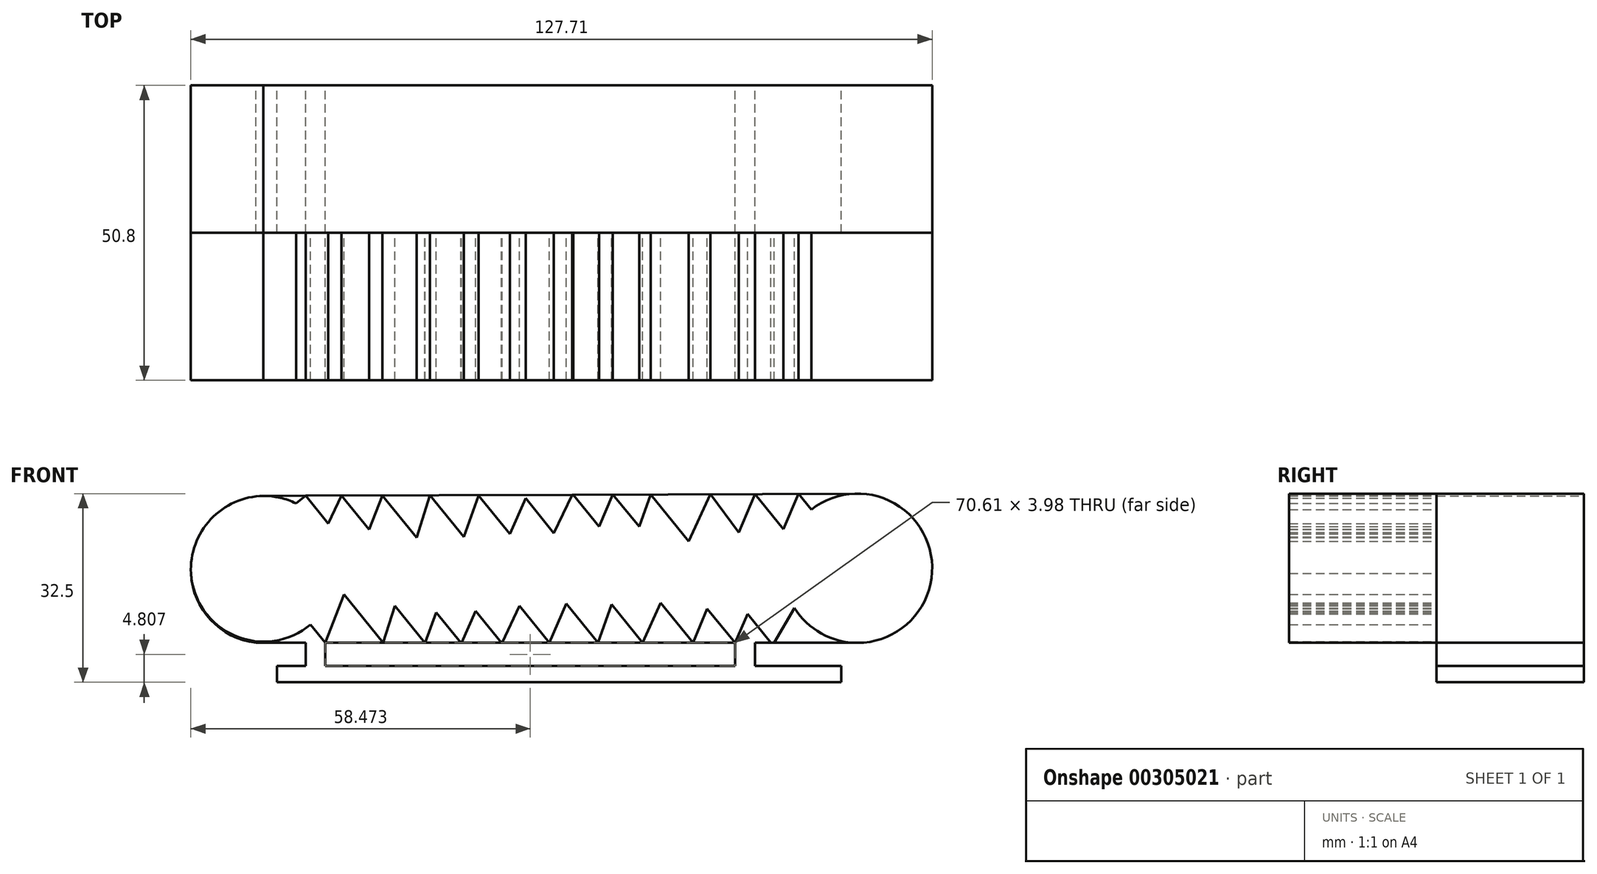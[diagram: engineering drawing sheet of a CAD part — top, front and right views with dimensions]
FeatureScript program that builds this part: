
annotation { "Feature Type Name" : "Feature", "Feature Type Description" : "" }
export const myFeature = defineFeature(function(context is Context, id is Id, definition is map)
    precondition{}
    {
        {
            var Q0;
            Q0=qCreatedBy(makeId("Front.planeOp"),FACE);
            var sketch = newSketch(context, id + "F0", { "sketchPlane" : qUnion([Q0])});
            skArc(sketch, "E0", {"start": v(-84.7, 31) * mm, "mid": v(-97.17, 18.95) * mm, "end": v(-85.99, 5.69) * mm});
            skLineSegment(sketch, "E1", {"start": v(-84.7, 31) * mm, "end": v(17.62, 31.4) * mm});
            skLineSegment(sketch, "E2", {"start": v(17.72, 5.69) * mm, "end": v(-85.99, 5.69) * mm});
            skArc(sketch, "E3", {"start": v(17.72, 5.69) * mm, "mid": v(30.52, 18.6) * mm, "end": v(17.62, 31.4) * mm});
            skLineSegment(sketch, "E4.bottom", {"start": v(-82.38, 1.7) * mm, "end": v(14.86, 1.7) * mm});
            skLineSegment(sketch, "E4.top", {"start": v(-82.38, -1.11) * mm, "end": v(14.86, -1.11) * mm});
            skLineSegment(sketch, "E4.left", {"start": v(-82.38, 1.7) * mm, "end": v(-82.38, -1.11) * mm});
            skLineSegment(sketch, "E4.right", {"start": v(14.86, 1.7) * mm, "end": v(14.86, -1.11) * mm});
            skLineSegment(sketch, "E5", {"start": v(-77.4, 5.69) * mm, "end": v(-77.4, 1.7) * mm});
            skLineSegment(sketch, "E6", {"start": v(-74.02, 5.69) * mm, "end": v(-74.02, 1.7) * mm});
            skLineSegment(sketch, "E7", {"start": v(-3.41, 5.69) * mm, "end": v(-3.41, 1.7) * mm});
            skLineSegment(sketch, "E8", {"start": v(0, 5.69) * mm, "end": v(0, 1.7) * mm});
            skSolve(sketch);
        }
        {
            var Q0;
            {var subQ4=sQuery(id+"F0.wireOp",EDGE,"E0");Q0=makeQuery(id+"F0.imprint","IMPRINT",FACE,{"disambiguationData":[TD([[makeQuery(id+"F0.imprint","IMPRINT",EDGE,{"derivedFrom":subQ4}),1.0]])]});}
            var Q1;
            Q1=makeQuery(id+"F0.imprint","IMPRINT",FACE,{"disambiguationData":[TD([[makeQuery(id+"F0.imprint","IMPRINT",EDGE,{"derivedFrom":sQuery(id+"F0.wireOp",EDGE,"E4.top")}),1.0]])]});
            var Q2;
            {var subQ0=sQuery(id+"F0.wireOp",EDGE,"E5");Q2=makeQuery(id+"F0.imprint","IMPRINT",FACE,{"disambiguationData":[TD([[makeQuery(id+"F0.imprint","IMPRINT",EDGE,{"derivedFrom":subQ0}),1.0]])]});}
            var Q3;
            {var subQ0=sQuery(id+"F0.wireOp",EDGE,"E7");Q3=makeQuery(id+"F0.imprint","IMPRINT",FACE,{"disambiguationData":[TD([[makeQuery(id+"F0.imprint","IMPRINT",EDGE,{"derivedFrom":subQ0}),1.0]])]});}
            extrude(context, id + "F1", {"entities" : qUnion([Q0, Q1, Q2, Q3]), "depth" : 25.4 * mm});
        }
        {
            var Q0;
            Q0=makeQuery(id+"F1.opExtrude","CAP_FACE",FACE,{"disambiguationData":[OSD([sQuery(id+"F0.wireOp",EDGE,"E0"),sQuery(id+"F0.wireOp",EDGE,"E1"),sQuery(id+"F0.wireOp",EDGE,"E2"),sQuery(id+"F0.wireOp",EDGE,"E3"),sQuery(id+"F0.wireOp",EDGE,"E4.bottom"),sQuery(id+"F0.wireOp",EDGE,"E4.top"),sQuery(id+"F0.wireOp",EDGE,"E4.left"),sQuery(id+"F0.wireOp",EDGE,"E4.right"),sQuery(id+"F0.wireOp",EDGE,"E5"),sQuery(id+"F0.wireOp",EDGE,"E6"),sQuery(id+"F0.wireOp",EDGE,"E7"),sQuery(id+"F0.wireOp",EDGE,"E8")])],"isStart":false});
            var sketch = newSketch(context, id + "F2", { "sketchPlane" : qUnion([Q0])});
            skArc(sketch, "E9", {"start": v(-97.17, 17.65) * mm, "mid": v(-75.47, 9.86) * mm, "end": v(-84.7, 31) * mm});
            skPoint(sketch, "E9.startSnap0", {"position": v(-97.17, 18.95) * mm});
            skArc(sketch, "E10", {"start": v(17.62, 31.4) * mm, "mid": v(10.72, 29.35) * mm, "end": v(6, 23.92) * mm});
            skPoint(sketch, "E10.endSnap0", {"position": v(30.52, 18.6) * mm});
            skLineSegment(sketch, "E11", {"start": v(-71.22, 31.05) * mm, "end": v(-50.7, 5.69) * mm});
            skLineSegment(sketch, "E12", {"start": v(-64.2, 31.08) * mm, "end": v(-43.65, 5.69) * mm});
            skLineSegment(sketch, "E13", {"start": v(-56, 31.1) * mm, "end": v(-35.42, 5.69) * mm});
            skLineSegment(sketch, "E14", {"start": v(-47.65, 31.14) * mm, "end": v(-27.06, 5.69) * mm});
            skLineSegment(sketch, "E15", {"start": v(-39.99, 31.17) * mm, "end": v(-19.37, 5.69) * mm});
            skLineSegment(sketch, "E16", {"start": v(-31.32, 31.2) * mm, "end": v(-10.67, 5.69) * mm});
            skPoint(sketch, "E17.end.orphan", {"position": v(-22.03, 31) * mm});
            skLineSegment(sketch, "E18", {"start": v(-24.5, 31.23) * mm, "end": v(-3.41, 5.69) * mm});
            skLineSegment(sketch, "E19", {"start": v(-17.95, 31.26) * mm, "end": v(2.74, 5.69) * mm});
            skLineSegment(sketch, "E20", {"start": v(-7.69, 31.3) * mm, "end": v(6.51, 12.15) * mm});
            skLineSegment(sketch, "E21", {"start": v(0, 31.33) * mm, "end": v(6, 23.92) * mm});
            skLineSegment(sketch, "E22", {"start": v(7.48, 31.35) * mm, "end": v(9.7, 28.62) * mm});
            skLineSegment(sketch, "E23", {"start": v(-77.4, 31.05) * mm, "end": v(-56.88, 5.69) * mm});
            skPoint(sketch, "E23.startSnap0", {"position": v(-77.4, 3.7) * mm});
            skLineSegment(sketch, "E24", {"start": v(-72.34, 15.93) * mm, "end": v(-64.05, 5.69) * mm});
            skLineSegment(sketch, "E25", {"start": v(-77.4, 9.86) * mm, "end": v(-74.02, 5.69) * mm});
            skPoint(sketch, "E25.startSnap0", {"position": v(-75.47, 9.86) * mm});
            skLineSegment(sketch, "E26", {"start": v(0, 31.33) * mm, "end": v(-10.67, 5.69) * mm});
            skLineSegment(sketch, "E27", {"start": v(-7.69, 31.3) * mm, "end": v(-19.37, 5.69) * mm});
            skLineSegment(sketch, "E28", {"start": v(-17.95, 31.26) * mm, "end": v(-27.06, 5.69) * mm});
            skLineSegment(sketch, "E29", {"start": v(-24.5, 31.23) * mm, "end": v(-35.42, 5.69) * mm});
            skLineSegment(sketch, "E30", {"start": v(-31.43, 31.4) * mm, "end": v(-43.65, 5.51) * mm});
            skLineSegment(sketch, "E31", {"start": v(-39.18, 31.29) * mm, "end": v(-50.69, 5.35) * mm});
            skLineSegment(sketch, "E32", {"start": v(-47.53, 31.26) * mm, "end": v(-56.96, 5.33) * mm});
            skLineSegment(sketch, "E33", {"start": v(6.9, 11.88) * mm, "end": v(3.07, 5.3) * mm});
            skLineSegment(sketch, "E34", {"start": v(6.44, 24.24) * mm, "end": v(5.34, 22.18) * mm});
            skLineSegment(sketch, "E35", {"start": v(-56, 31.1) * mm, "end": v(-64.05, 5.69) * mm});
            skLineSegment(sketch, "E36", {"start": v(-64.2, 31.08) * mm, "end": v(-74.02, 5.69) * mm});
            skPoint(sketch, "E37.end.orphan", {"position": v(-72.34, 22.47) * mm});
            skPoint(sketch, "E38.trimOffspring.end.orphan", {"position": v(-74.02, 25.13) * mm});
            skPoint(sketch, "E39.end.orphan", {"position": v(-74.02, 22.7) * mm});
            skLineSegment(sketch, "E40", {"start": v(-71.22, 31.05) * mm, "end": v(-74.02, 25.13) * mm});
            skLineSegment(sketch, "E41", {"start": v(-77.4, 31.05) * mm, "end": v(-79.08, 29.7) * mm});
            skArc(sketch, "E42.trimOffspring", {"start": v(5.34, 22.18) * mm, "mid": v(15.8, 5.82) * mm, "end": v(30.52, 18.5) * mm});
            skLineSegment(sketch, "E43", {"start": v(7.48, 31.35) * mm, "end": v(-3.41, 5.69) * mm});
            skSolve(sketch);
        }
        {
            var Q0;
            {var subQ3=sQuery(id+"F2.wireOp",EDGE,"E22");Q0=makeQuery(id+"F2.imprint","IMPRINT",FACE,{"disambiguationData":[TD([[makeQuery(id+"F2.imprint","IMPRINT",EDGE,{"derivedFrom":subQ3}),-1.0]])]});}
            var Q1;
            {var subQ0=sQuery(id+"F2.wireOp",EDGE,"E24");var subQ1=sQuery(id+"F2.wireOp",EDGE,"E9");var subQ2=makeQuery(id+"F2.imprint","INTERSECT",VERTEX,{"derivedFrom":[subQ1,subQ0]});Q1=makeQuery(id+"F2.imprint","IMPRINT",FACE,{"disambiguationData":[TD([[makeQuery(id+"F2.imprint","IMPRINT",EDGE,{"disambiguationData":[TD([[subQ2,1.0]])],"derivedFrom":subQ1}),-1.0]])]});}
            var Q2;
            {var subQ0=sQuery(id+"F2.wireOp",EDGE,"E40");var subQ5=sQuery(id+"F2.wireOp",EDGE,"E23");var subQ6=makeQuery(id+"F2.imprint","INTERSECT",VERTEX,{"derivedFrom":[subQ5,subQ0]});Q2=makeQuery(id+"F2.imprint","IMPRINT",FACE,{"disambiguationData":[TD([[makeQuery(id+"F2.imprint","IMPRINT",EDGE,{"disambiguationData":[TD([[subQ6,-1.0]])],"derivedFrom":subQ5}),1.0]])]});}
            var Q3;
            {var subQ0=sQuery(id+"F2.wireOp",EDGE,"E36");var subQ1=sQuery(id+"F2.wireOp",EDGE,"E11");var subQ2=makeQuery(id+"F2.imprint","INTERSECT",VERTEX,{"derivedFrom":[subQ1,subQ0]});Q3=makeQuery(id+"F2.imprint","IMPRINT",FACE,{"disambiguationData":[TD([[makeQuery(id+"F2.imprint","IMPRINT",EDGE,{"disambiguationData":[TD([[subQ2,-1.0]])],"derivedFrom":subQ1}),1.0]])]});}
            var Q4;
            {var subQ0=sQuery(id+"F2.wireOp",EDGE,"E36");var subQ1=sQuery(id+"F2.wireOp",EDGE,"E11");var subQ2=makeQuery(id+"F2.imprint","INTERSECT",VERTEX,{"derivedFrom":[subQ1,subQ0]});Q4=makeQuery(id+"F2.imprint","IMPRINT",FACE,{"disambiguationData":[TD([[makeQuery(id+"F2.imprint","IMPRINT",EDGE,{"disambiguationData":[TD([[subQ2,-1.0]])],"derivedFrom":subQ1}),-1.0]])]});}
            var Q5;
            {var subQ0=sQuery(id+"F2.wireOp",EDGE,"E35");var subQ1=sQuery(id+"F2.wireOp",EDGE,"E11");var subQ2=makeQuery(id+"F2.imprint","INTERSECT",VERTEX,{"derivedFrom":[subQ1,subQ0]});Q5=makeQuery(id+"F2.imprint","IMPRINT",FACE,{"disambiguationData":[TD([[makeQuery(id+"F2.imprint","IMPRINT",EDGE,{"disambiguationData":[TD([[subQ2,-1.0]])],"derivedFrom":subQ1}),1.0]])]});}
            var Q6;
            {var subQ0=sQuery(id+"F2.wireOp",EDGE,"E35");var subQ1=sQuery(id+"F2.wireOp",EDGE,"E12");var subQ2=makeQuery(id+"F2.imprint","INTERSECT",VERTEX,{"derivedFrom":[subQ1,subQ0]});Q6=makeQuery(id+"F2.imprint","IMPRINT",FACE,{"disambiguationData":[TD([[makeQuery(id+"F2.imprint","IMPRINT",EDGE,{"disambiguationData":[TD([[subQ2,-1.0]])],"derivedFrom":subQ1}),1.0]])]});}
            var Q7;
            {var subQ0=sQuery(id+"F2.wireOp",EDGE,"E32");var subQ1=sQuery(id+"F2.wireOp",EDGE,"E12");var subQ2=makeQuery(id+"F2.imprint","INTERSECT",VERTEX,{"derivedFrom":[subQ1,subQ0]});Q7=makeQuery(id+"F2.imprint","IMPRINT",FACE,{"disambiguationData":[TD([[makeQuery(id+"F2.imprint","IMPRINT",EDGE,{"disambiguationData":[TD([[subQ2,-1.0]])],"derivedFrom":subQ1}),1.0]])]});}
            var Q8;
            {var subQ0=sQuery(id+"F2.wireOp",EDGE,"E32");var subQ1=sQuery(id+"F2.wireOp",EDGE,"E13");var subQ2=makeQuery(id+"F2.imprint","INTERSECT",VERTEX,{"derivedFrom":[subQ1,subQ0]});Q8=makeQuery(id+"F2.imprint","IMPRINT",FACE,{"disambiguationData":[TD([[makeQuery(id+"F2.imprint","IMPRINT",EDGE,{"disambiguationData":[TD([[subQ2,-1.0]])],"derivedFrom":subQ1}),1.0]])]});}
            var Q9;
            {var subQ0=sQuery(id+"F2.wireOp",EDGE,"E31");var subQ1=sQuery(id+"F2.wireOp",EDGE,"E13");var subQ2=makeQuery(id+"F2.imprint","INTERSECT",VERTEX,{"derivedFrom":[subQ1,subQ0]});Q9=makeQuery(id+"F2.imprint","IMPRINT",FACE,{"disambiguationData":[TD([[makeQuery(id+"F2.imprint","IMPRINT",EDGE,{"disambiguationData":[TD([[subQ2,-1.0]])],"derivedFrom":subQ1}),1.0]])]});}
            var Q10;
            {var subQ4=sQuery(id+"F2.wireOp",EDGE,"E30");var subQ6=sQuery(id+"F2.wireOp",EDGE,"E14");var subQ7=makeQuery(id+"F2.imprint","INTERSECT",VERTEX,{"derivedFrom":[subQ6,subQ4]});Q10=makeQuery(id+"F2.imprint","IMPRINT",FACE,{"disambiguationData":[TD([[makeQuery(id+"F2.imprint","IMPRINT",EDGE,{"disambiguationData":[TD([[subQ7,-1.0]])],"derivedFrom":subQ6}),-1.0]])]});}
            var Q11;
            {var subQ0=sQuery(id+"F2.wireOp",EDGE,"E31");var subQ1=sQuery(id+"F2.wireOp",EDGE,"E14");var subQ2=makeQuery(id+"F2.imprint","INTERSECT",VERTEX,{"derivedFrom":[subQ1,subQ0]});Q11=makeQuery(id+"F2.imprint","IMPRINT",FACE,{"disambiguationData":[TD([[makeQuery(id+"F2.imprint","IMPRINT",EDGE,{"disambiguationData":[TD([[subQ2,-1.0]])],"derivedFrom":subQ1}),1.0]])]});}
            var Q12;
            {var subQ0=sQuery(id+"F2.wireOp",EDGE,"E30");var subQ1=sQuery(id+"F2.wireOp",EDGE,"E14");var subQ2=makeQuery(id+"F2.imprint","INTERSECT",VERTEX,{"derivedFrom":[subQ1,subQ0]});Q12=makeQuery(id+"F2.imprint","IMPRINT",FACE,{"disambiguationData":[TD([[makeQuery(id+"F2.imprint","IMPRINT",EDGE,{"disambiguationData":[TD([[subQ2,-1.0]])],"derivedFrom":subQ1}),1.0]])]});}
            var Q13;
            {var subQ4=sQuery(id+"F2.wireOp",EDGE,"E29");var subQ6=sQuery(id+"F2.wireOp",EDGE,"E15");var subQ7=makeQuery(id+"F2.imprint","INTERSECT",VERTEX,{"derivedFrom":[subQ6,subQ4]});Q13=makeQuery(id+"F2.imprint","IMPRINT",FACE,{"disambiguationData":[TD([[makeQuery(id+"F2.imprint","IMPRINT",EDGE,{"disambiguationData":[TD([[subQ7,-1.0]])],"derivedFrom":subQ6}),-1.0]])]});}
            var Q14;
            {var subQ0=sQuery(id+"F2.wireOp",EDGE,"E29");var subQ1=sQuery(id+"F2.wireOp",EDGE,"E15");var subQ2=makeQuery(id+"F2.imprint","INTERSECT",VERTEX,{"derivedFrom":[subQ1,subQ0]});Q14=makeQuery(id+"F2.imprint","IMPRINT",FACE,{"disambiguationData":[TD([[makeQuery(id+"F2.imprint","IMPRINT",EDGE,{"disambiguationData":[TD([[subQ2,-1.0]])],"derivedFrom":subQ1}),1.0]])]});}
            var Q15;
            {var subQ0=sQuery(id+"F2.wireOp",EDGE,"E29");var subQ1=sQuery(id+"F2.wireOp",EDGE,"E16");var subQ2=makeQuery(id+"F2.imprint","INTERSECT",VERTEX,{"derivedFrom":[subQ1,subQ0]});Q15=makeQuery(id+"F2.imprint","IMPRINT",FACE,{"disambiguationData":[TD([[makeQuery(id+"F2.imprint","IMPRINT",EDGE,{"disambiguationData":[TD([[subQ2,-1.0]])],"derivedFrom":subQ1}),1.0]])]});}
            var Q16;
            {var subQ0=sQuery(id+"F2.wireOp",EDGE,"E27");var subQ1=sQuery(id+"F2.wireOp",EDGE,"E16");var subQ2=makeQuery(id+"F2.imprint","INTERSECT",VERTEX,{"derivedFrom":[subQ1,subQ0]});Q16=makeQuery(id+"F2.imprint","IMPRINT",FACE,{"disambiguationData":[TD([[makeQuery(id+"F2.imprint","IMPRINT",EDGE,{"disambiguationData":[TD([[subQ2,1.0]])],"derivedFrom":subQ1}),1.0]])]});}
            var Q17;
            {var subQ4=sQuery(id+"F2.wireOp",EDGE,"E27");var subQ6=sQuery(id+"F2.wireOp",EDGE,"E18");var subQ7=makeQuery(id+"F2.imprint","INTERSECT",VERTEX,{"derivedFrom":[subQ6,subQ4]});Q17=makeQuery(id+"F2.imprint","IMPRINT",FACE,{"disambiguationData":[TD([[makeQuery(id+"F2.imprint","IMPRINT",EDGE,{"disambiguationData":[TD([[subQ7,-1.0]])],"derivedFrom":subQ6}),-1.0]])]});}
            var Q18;
            {var subQ0=sQuery(id+"F2.wireOp",EDGE,"E28");var subQ1=sQuery(id+"F2.wireOp",EDGE,"E18");var subQ2=makeQuery(id+"F2.imprint","INTERSECT",VERTEX,{"derivedFrom":[subQ1,subQ0]});Q18=makeQuery(id+"F2.imprint","IMPRINT",FACE,{"disambiguationData":[TD([[makeQuery(id+"F2.imprint","IMPRINT",EDGE,{"disambiguationData":[TD([[subQ2,-1.0]])],"derivedFrom":subQ1}),1.0]])]});}
            var Q19;
            {var subQ0=sQuery(id+"F2.wireOp",EDGE,"E27");var subQ1=sQuery(id+"F2.wireOp",EDGE,"E18");var subQ2=makeQuery(id+"F2.imprint","INTERSECT",VERTEX,{"derivedFrom":[subQ1,subQ0]});Q19=makeQuery(id+"F2.imprint","IMPRINT",FACE,{"disambiguationData":[TD([[makeQuery(id+"F2.imprint","IMPRINT",EDGE,{"disambiguationData":[TD([[subQ2,-1.0]])],"derivedFrom":subQ1}),1.0]])]});}
            var Q20;
            {var subQ5=sQuery(id+"F2.wireOp",EDGE,"E26");var subQ7=sQuery(id+"F2.wireOp",EDGE,"E19");var subQ8=makeQuery(id+"F2.imprint","INTERSECT",VERTEX,{"derivedFrom":[subQ7,subQ5]});Q20=makeQuery(id+"F2.imprint","IMPRINT",FACE,{"disambiguationData":[TD([[makeQuery(id+"F2.imprint","IMPRINT",EDGE,{"disambiguationData":[TD([[subQ8,-1.0]])],"derivedFrom":subQ7}),-1.0]])]});}
            var Q21;
            {var subQ0=sQuery(id+"F2.wireOp",EDGE,"E27");var subQ1=sQuery(id+"F2.wireOp",EDGE,"E19");var subQ2=makeQuery(id+"F2.imprint","INTERSECT",VERTEX,{"derivedFrom":[subQ1,subQ0]});Q21=makeQuery(id+"F2.imprint","IMPRINT",FACE,{"disambiguationData":[TD([[makeQuery(id+"F2.imprint","IMPRINT",EDGE,{"disambiguationData":[TD([[subQ2,-1.0]])],"derivedFrom":subQ1}),1.0]])]});}
            var Q22;
            {var subQ0=sQuery(id+"F2.wireOp",EDGE,"E26");var subQ1=sQuery(id+"F2.wireOp",EDGE,"E20");var subQ2=makeQuery(id+"F2.imprint","INTERSECT",VERTEX,{"derivedFrom":[subQ1,subQ0]});Q22=makeQuery(id+"F2.imprint","IMPRINT",FACE,{"disambiguationData":[TD([[makeQuery(id+"F2.imprint","IMPRINT",EDGE,{"disambiguationData":[TD([[subQ2,-1.0]])],"derivedFrom":subQ1}),1.0]])]});}
            var Q23;
            {var subQ0=sQuery(id+"F2.wireOp",EDGE,"E36");var subQ1=sQuery(id+"F2.wireOp",EDGE,"E23");var subQ2=makeQuery(id+"F2.imprint","INTERSECT",VERTEX,{"derivedFrom":[subQ1,subQ0]});Q23=makeQuery(id+"F2.imprint","IMPRINT",FACE,{"disambiguationData":[TD([[makeQuery(id+"F2.imprint","IMPRINT",EDGE,{"disambiguationData":[TD([[subQ2,-1.0]])],"derivedFrom":subQ1}),-1.0]])]});}
            var Q24;
            {var subQ3=sQuery(id+"F2.wireOp",EDGE,"E24");var subQ7=sQuery(id+"F2.wireOp",EDGE,"E9");var subQ8=makeQuery(id+"F2.imprint","INTERSECT",VERTEX,{"derivedFrom":[subQ7,subQ3]});Q24=makeQuery(id+"F2.imprint","IMPRINT",FACE,{"disambiguationData":[TD([[makeQuery(id+"F2.imprint","IMPRINT",EDGE,{"disambiguationData":[TD([[subQ8,-1.0]])],"derivedFrom":subQ7}),-1.0]])]});}
            var Q25;
            {var subQ0=sQuery(id+"F2.wireOp",EDGE,"E41");var subQ1=sQuery(id+"F2.wireOp",EDGE,"E23");var subQ2=makeQuery(id+"F2.imprint","INTERSECT",VERTEX,{"derivedFrom":[subQ1,subQ0]});Q25=makeQuery(id+"F2.imprint","IMPRINT",FACE,{"disambiguationData":[TD([[makeQuery(id+"F2.imprint","IMPRINT",EDGE,{"disambiguationData":[TD([[subQ2,-1.0]])],"derivedFrom":subQ1}),-1.0]])]});}
            var Q26;
            {var subQ0=sQuery(id+"F2.wireOp",EDGE,"E42.trimOffspring");var subQ1=sQuery(id+"F0.wireOp",EDGE,"E2");var subQ2=makeQuery(id+"F1.opExtrude","CAP_EDGE",EDGE,{"disambiguationData":[OSD([subQ1]),TDD([makeQuery(id+"F0.imprint","IMPRINT",EDGE,{"disambiguationData":[TD([[makeQuery(id+"F0.imprint","INTERSECT",VERTEX,{"derivedFrom":[subQ1,sQuery(id+"F0.wireOp",EDGE,"E3")]}),-1.0]])],"derivedFrom":subQ1})])],"isStart":false});var subQ3=makeQuery(id+"F2.imprint","INTERSECT",VERTEX,{"disambiguationData":[OD(0.0)],"derivedFrom":[subQ2,subQ0]});Q26=makeQuery(id+"F2.imprint","IMPRINT",FACE,{"disambiguationData":[TD([[makeQuery(id+"F2.imprint","IMPRINT",EDGE,{"disambiguationData":[TD([[subQ3,1.0]])],"derivedFrom":subQ0}),1.0]])]});}
            var Q27;
            {var subQ1=sQuery(id+"F2.wireOp",EDGE,"E9");var subQ5=sQuery(id+"F2.wireOp",EDGE,"E40");var subQ6=makeQuery(id+"F2.imprint","INTERSECT",VERTEX,{"derivedFrom":[subQ1,subQ5]});Q27=makeQuery(id+"F2.imprint","IMPRINT",FACE,{"disambiguationData":[TD([[makeQuery(id+"F2.imprint","IMPRINT",EDGE,{"disambiguationData":[TD([[subQ6,-1.0]])],"derivedFrom":subQ1}),-1.0]])]});}
            var Q28;
            {var subQ6=sQuery(id+"F2.wireOp",EDGE,"E21");var subQ7=sQuery(id+"F2.wireOp",EDGE,"E10");var subQ8=makeQuery(id+"F2.imprint","INTERSECT",VERTEX,{"derivedFrom":[subQ7,subQ6]});Q28=makeQuery(id+"F2.imprint","IMPRINT",FACE,{"disambiguationData":[TD([[makeQuery(id+"F2.imprint","IMPRINT",EDGE,{"disambiguationData":[TD([[subQ8,1.0]])],"derivedFrom":subQ7}),1.0]])]});}
            var Q29;
            {var subQ0=sQuery(id+"F2.wireOp",EDGE,"E9");var subQ5=makeQuery(id+"F1.opExtrude","CAP_EDGE",EDGE,{"disambiguationData":[OSD([sQuery(id+"F0.wireOp",EDGE,"E0")])],"isStart":false});var subQ6=makeQuery(id+"F2.imprint","INTERSECT",VERTEX,{"derivedFrom":[subQ5,subQ0]});Q29=makeQuery(id+"F2.imprint","IMPRINT",FACE,{"disambiguationData":[TD([[makeQuery(id+"F2.imprint","IMPRINT",EDGE,{"disambiguationData":[TD([[subQ6,-1.0]])],"derivedFrom":subQ0}),1.0]])]});}
            var Q30;
            {var subQ0=sQuery(id+"F2.wireOp",EDGE,"E35");var subQ1=sQuery(id+"F2.wireOp",EDGE,"E11");var subQ2=makeQuery(id+"F2.imprint","INTERSECT",VERTEX,{"derivedFrom":[subQ1,subQ0]});Q30=makeQuery(id+"F2.imprint","IMPRINT",FACE,{"disambiguationData":[TD([[makeQuery(id+"F2.imprint","IMPRINT",EDGE,{"disambiguationData":[TD([[subQ2,-1.0]])],"derivedFrom":subQ1}),-1.0]])]});}
            var Q31;
            {var subQ0=sQuery(id+"F2.wireOp",EDGE,"E32");var subQ3=sQuery(id+"F2.wireOp",EDGE,"E12");var subQ4=makeQuery(id+"F2.imprint","INTERSECT",VERTEX,{"derivedFrom":[subQ3,subQ0]});Q31=makeQuery(id+"F2.imprint","IMPRINT",FACE,{"disambiguationData":[TD([[makeQuery(id+"F2.imprint","IMPRINT",EDGE,{"disambiguationData":[TD([[subQ4,-1.0]])],"derivedFrom":subQ3}),-1.0]])]});}
            var Q32;
            {var subQ1=sQuery(id+"F2.wireOp",EDGE,"E13");var subQ6=sQuery(id+"F2.wireOp",EDGE,"E31");var subQ9=makeQuery(id+"F2.imprint","INTERSECT",VERTEX,{"derivedFrom":[subQ1,subQ6]});Q32=makeQuery(id+"F2.imprint","IMPRINT",FACE,{"disambiguationData":[TD([[makeQuery(id+"F2.imprint","IMPRINT",EDGE,{"disambiguationData":[TD([[subQ9,-1.0]])],"derivedFrom":subQ1}),-1.0]])]});}
            var Q33;
            {var subQ0=sQuery(id+"F2.wireOp",EDGE,"E42.trimOffspring");var subQ10=sQuery(id+"F2.wireOp",EDGE,"E20");var subQ11=makeQuery(id+"F2.imprint","INTERSECT",VERTEX,{"derivedFrom":[subQ10,subQ0]});Q33=makeQuery(id+"F2.imprint","IMPRINT",FACE,{"disambiguationData":[TD([[makeQuery(id+"F2.imprint","IMPRINT",EDGE,{"disambiguationData":[TD([[subQ11,1.0]])],"derivedFrom":subQ10}),-1.0]])]});}
            var Q34;
            {var subQ0=sQuery(id+"F2.wireOp",EDGE,"E26");var subQ1=sQuery(id+"F2.wireOp",EDGE,"E19");var subQ2=makeQuery(id+"F2.imprint","INTERSECT",VERTEX,{"derivedFrom":[subQ1,subQ0]});Q34=makeQuery(id+"F2.imprint","IMPRINT",FACE,{"disambiguationData":[TD([[makeQuery(id+"F2.imprint","IMPRINT",EDGE,{"disambiguationData":[TD([[subQ2,-1.0]])],"derivedFrom":subQ1}),1.0]])]});}
            var Q35;
            {var subQ3=sQuery(id+"F2.wireOp",EDGE,"E16");var subQ5=makeQuery(id+"F2.imprint","INTERSECT",VERTEX,{"derivedFrom":[subQ3,sQuery(id+"F2.wireOp",EDGE,"E27")]});Q35=makeQuery(id+"F2.imprint","IMPRINT",FACE,{"disambiguationData":[TD([[makeQuery(id+"F2.imprint","IMPRINT",EDGE,{"disambiguationData":[TD([[subQ5,1.0]])],"derivedFrom":subQ3}),-1.0]])]});}
            var Q36;
            {var subQ0=sQuery(id+"F2.wireOp",EDGE,"E30");var subQ1=sQuery(id+"F2.wireOp",EDGE,"E15");var subQ2=makeQuery(id+"F2.imprint","INTERSECT",VERTEX,{"derivedFrom":[subQ1,subQ0]});Q36=makeQuery(id+"F2.imprint","IMPRINT",FACE,{"disambiguationData":[TD([[makeQuery(id+"F2.imprint","IMPRINT",EDGE,{"disambiguationData":[TD([[subQ2,-1.0]])],"derivedFrom":subQ1}),1.0]])]});}
            extrude(context, id + "F3", {"entities" : qUnion([Q0, Q1, Q2, Q3, Q4, Q5, Q6, Q7, Q8, Q9, Q10, Q11, Q12, Q13, Q14, Q15, Q16, Q17, Q18, Q19, Q20, Q21, Q22, Q23, Q24, Q25, Q26, Q27, Q28, Q29, Q30, Q31, Q32, Q33, Q34, Q35, Q36]), "depth" : 25.4 * mm});
        }
    });
